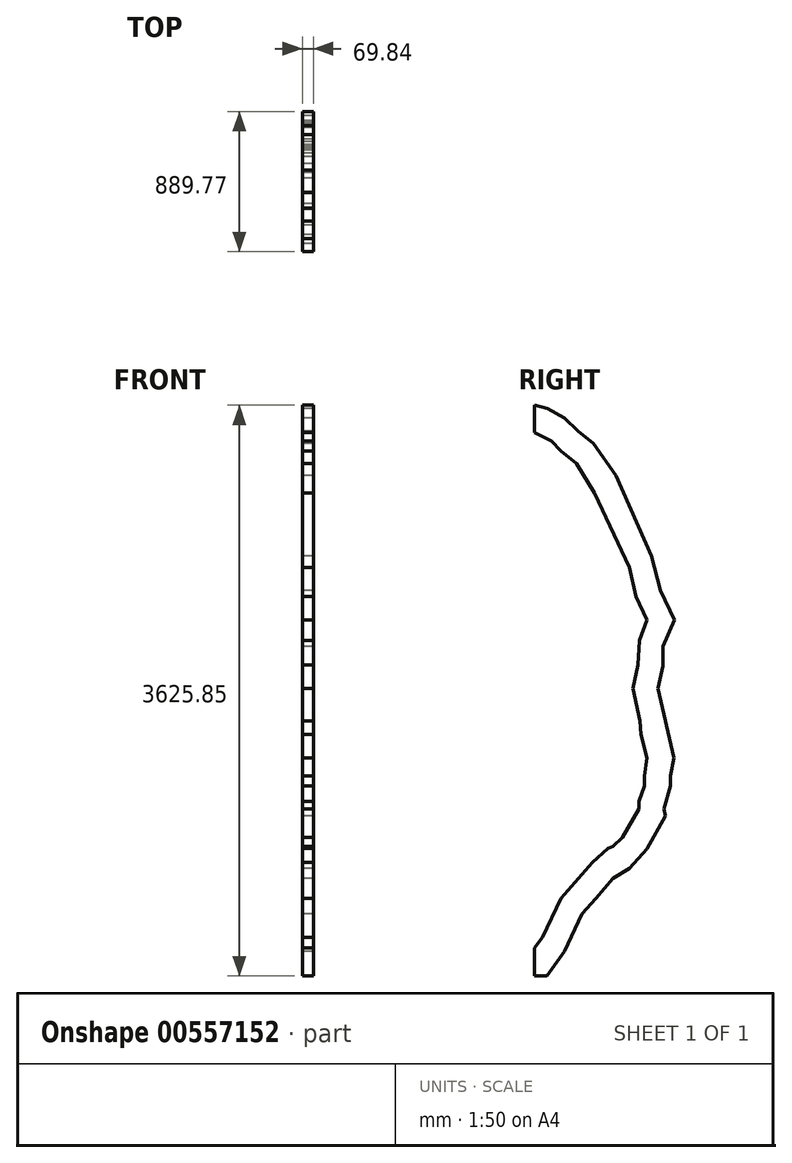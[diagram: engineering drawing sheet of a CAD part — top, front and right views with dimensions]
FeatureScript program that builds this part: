
annotation { "Feature Type Name" : "Feature", "Feature Type Description" : "" }
export const myFeature = defineFeature(function(context is Context, id is Id, definition is map)
    precondition{}
    {
        {
            var Q0;
            Q0=qCreatedBy(makeId("Right.planeOp"),FACE);
            var sketch = newSketch(context, id + "F0", { "sketchPlane" : qUnion([Q0])});
            skLineSegment(sketch, "E0", {"start": v(0, 0) * mm, "end": v(0, 177.5) * mm});
            skLineSegment(sketch, "E1", {"start": v(0, 177.5) * mm, "end": v(52.5, 244.77) * mm});
            skLineSegment(sketch, "E2", {"start": v(52.5, 244.77) * mm, "end": v(169, 492.47) * mm});
            skLineSegment(sketch, "E3", {"start": v(169, 492.47) * mm, "end": v(370.77, 721.9) * mm});
            skLineSegment(sketch, "E4", {"start": v(370.77, 721.9) * mm, "end": v(468.78, 809.53) * mm});
            skLineSegment(sketch, "E5", {"start": v(468.78, 809.53) * mm, "end": v(501.06, 824.53) * mm});
            skLineSegment(sketch, "E6", {"start": v(501.06, 824.53) * mm, "end": v(558.8, 881.1) * mm});
            skLineSegment(sketch, "E7", {"start": v(558.8, 881.1) * mm, "end": v(665.05, 1062.54) * mm});
            skLineSegment(sketch, "E8", {"start": v(665.05, 1062.54) * mm, "end": v(665.05, 1110.05) * mm});
            skLineSegment(sketch, "E9", {"start": v(665.05, 1110.05) * mm, "end": v(699.88, 1205.94) * mm});
            skLineSegment(sketch, "E10", {"start": v(699.88, 1205.94) * mm, "end": v(699.88, 1271.85) * mm});
            skLineSegment(sketch, "E11", {"start": v(699.88, 1271.85) * mm, "end": v(716.02, 1386.23) * mm});
            skLineSegment(sketch, "E12", {"start": v(716.02, 1386.23) * mm, "end": v(679.3, 1533.5) * mm});
            skLineSegment(sketch, "E13", {"start": v(679.3, 1533.5) * mm, "end": v(672.52, 1621.58) * mm});
            skLineSegment(sketch, "E14", {"start": v(672.52, 1621.58) * mm, "end": v(625.82, 1827.22) * mm});
            skLineSegment(sketch, "E15", {"start": v(625.82, 1827.22) * mm, "end": v(658.75, 1976.86) * mm});
            skLineSegment(sketch, "E16", {"start": v(658.75, 1976.86) * mm, "end": v(667.07, 2131.5) * mm});
            skLineSegment(sketch, "E17", {"start": v(667.07, 2131.5) * mm, "end": v(716.02, 2260.52) * mm});
            skLineSegment(sketch, "E18", {"start": v(716.02, 2260.52) * mm, "end": v(645.65, 2410.87) * mm});
            skLineSegment(sketch, "E19", {"start": v(645.65, 2410.87) * mm, "end": v(604.04, 2594.1) * mm});
            skLineSegment(sketch, "E20", {"start": v(604.04, 2594.1) * mm, "end": v(381.62, 3069.3) * mm});
            skLineSegment(sketch, "E21", {"start": v(381.62, 3069.3) * mm, "end": v(266.9, 3255.13) * mm});
            skLineSegment(sketch, "E22", {"start": v(266.9, 3255.13) * mm, "end": v(169, 3333.01) * mm});
            skLineSegment(sketch, "E23", {"start": v(169, 3333.01) * mm, "end": v(108.57, 3396.86) * mm});
            skLineSegment(sketch, "E24", {"start": v(108.57, 3396.86) * mm, "end": v(0, 3453) * mm});
            skLineSegment(sketch, "E25", {"start": v(0, 3453) * mm, "end": v(0, 3625.85) * mm});
            skLineSegment(sketch, "E26", {"start": v(0, 3625.85) * mm, "end": v(83.25, 3606.03) * mm});
            skLineSegment(sketch, "E27", {"start": v(83.25, 3606.03) * mm, "end": v(193.34, 3543.28) * mm});
            skLineSegment(sketch, "E28", {"start": v(193.34, 3543.28) * mm, "end": v(278.11, 3460.72) * mm});
            skLineSegment(sketch, "E29", {"start": v(278.11, 3460.72) * mm, "end": v(376.1, 3382.55) * mm});
            skLineSegment(sketch, "E30", {"start": v(376.1, 3382.55) * mm, "end": v(518.1, 3177.78) * mm});
            skLineSegment(sketch, "E31", {"start": v(518.1, 3177.78) * mm, "end": v(744.6, 2669.38) * mm});
            skLineSegment(sketch, "E32", {"start": v(744.6, 2669.38) * mm, "end": v(801.54, 2449.04) * mm});
            skLineSegment(sketch, "E33", {"start": v(801.54, 2449.04) * mm, "end": v(889.77, 2260.52) * mm});
            skLineSegment(sketch, "E34", {"start": v(889.77, 2260.52) * mm, "end": v(816.84, 2091.58) * mm});
            skLineSegment(sketch, "E35", {"start": v(816.84, 2091.58) * mm, "end": v(816.84, 1970.75) * mm});
            skLineSegment(sketch, "E36", {"start": v(816.84, 1970.75) * mm, "end": v(786.63, 1827.22) * mm});
            skLineSegment(sketch, "E37", {"start": v(786.63, 1827.22) * mm, "end": v(830.87, 1632.43) * mm});
            skLineSegment(sketch, "E38", {"start": v(830.87, 1632.43) * mm, "end": v(853.33, 1533.5) * mm});
            skLineSegment(sketch, "E39", {"start": v(853.33, 1533.5) * mm, "end": v(886.78, 1386.23) * mm});
            skLineSegment(sketch, "E40", {"start": v(886.78, 1386.23) * mm, "end": v(864.3, 1271.85) * mm});
            skLineSegment(sketch, "E41", {"start": v(864.3, 1271.85) * mm, "end": v(864.3, 1205.94) * mm});
            skLineSegment(sketch, "E42", {"start": v(864.3, 1205.94) * mm, "end": v(823.31, 1060.19) * mm});
            skLineSegment(sketch, "E43", {"start": v(823.31, 1060.19) * mm, "end": v(833.46, 1015.51) * mm});
            skLineSegment(sketch, "E44", {"start": v(833.46, 1015.51) * mm, "end": v(716.02, 805.92) * mm});
            skLineSegment(sketch, "E45", {"start": v(716.02, 805.92) * mm, "end": v(604.27, 682.35) * mm});
            skLineSegment(sketch, "E46", {"start": v(604.27, 682.35) * mm, "end": v(558.8, 654.27) * mm});
            skLineSegment(sketch, "E47", {"start": v(558.8, 654.27) * mm, "end": v(501.06, 618.63) * mm});
            skLineSegment(sketch, "E48", {"start": v(501.06, 618.63) * mm, "end": v(390.52, 492.47) * mm});
            skLineSegment(sketch, "E49", {"start": v(390.52, 492.47) * mm, "end": v(304.22, 393.24) * mm});
            skLineSegment(sketch, "E50", {"start": v(304.22, 393.24) * mm, "end": v(191.17, 157.1) * mm});
            skLineSegment(sketch, "E51", {"start": v(191.17, 157.1) * mm, "end": v(80.63, 0) * mm});
            skLineSegment(sketch, "E52", {"start": v(80.63, 0) * mm, "end": v(0, 0) * mm});
            skSolve(sketch);
        }
        {
            var Q0;
            Q0 = qSketchRegion(id + "F0", true);
            extrude(context, id + "F1", {"entities" : qUnion([Q0]), "depth" : 69.85 * mm, "offsetDistance" : 25.4 * mm, "symmetric" : true});
        }
    });
